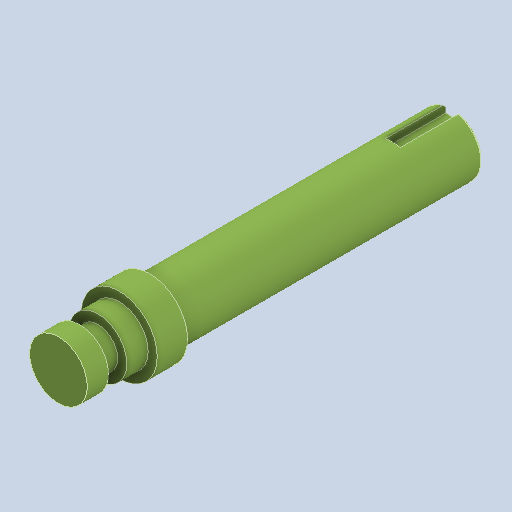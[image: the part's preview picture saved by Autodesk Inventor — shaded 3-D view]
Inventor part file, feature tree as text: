
AUTODESK INVENTOR PART (.ipt)
format: ipt  version: 2022 (Build 260153000, 153)  size: 127,488 bytes
history: native  units: in
note: dims shown in document units (in); Inventor stores cm internally (conversion verified against a paired STEP export)
features: sketch x6, other x3
ambient origin geometry x8: Origin, YZ Plane, XZ Plane, XY Plane, X Axis, Y Axis, Z Axis, Center Point
bodies: Solid1 (feature_tree)
feature tree (9):
  other  "shaft.ipt"
  other  "Solid1::shaft.ipt"
  other  "TaggingFeature1"
  sketch  "Sketch1"  dims[d0=0.3937in]
  sketch  "Sketch2"
  sketch  "Sketch3"
  sketch  "Sketch4"
  sketch  "Sketch5"
  sketch  "Sketch6"
